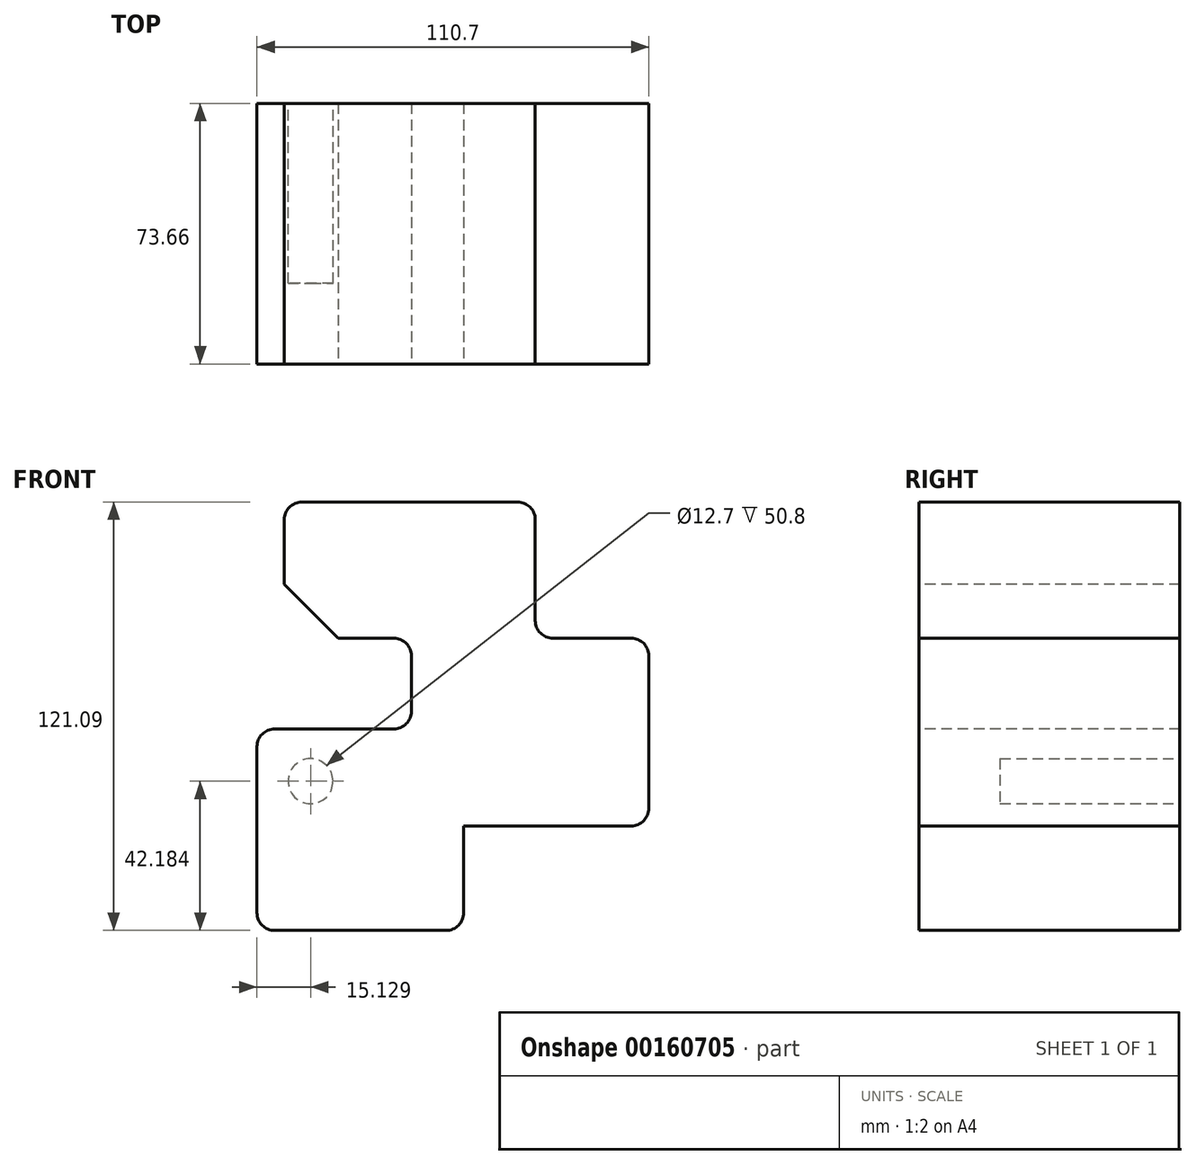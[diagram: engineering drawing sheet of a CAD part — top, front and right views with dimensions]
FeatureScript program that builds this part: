
annotation { "Feature Type Name" : "Feature", "Feature Type Description" : "" }
export const myFeature = defineFeature(function(context is Context, id is Id, definition is map)
    precondition{}
    {
        {
            var Q0;
            Q0=qCreatedBy(makeId("Front.planeOp"),FACE);
            var sketch = newSketch(context, id + "F0", { "sketchPlane" : qUnion([Q0])});
            skLineSegment(sketch, "E0", {"start": v(-32.8, 8.86) * mm, "end": v(-32.8, 47.35) * mm});
            skLineSegment(sketch, "E1", {"start": v(-32.8, 47.35) * mm, "end": v(38.1, 47.35) * mm});
            skLineSegment(sketch, "E2", {"start": v(38.1, 47.35) * mm, "end": v(38.1, 8.86) * mm});
            skLineSegment(sketch, "E3", {"start": v(38.1, 8.86) * mm, "end": v(70.2, 8.86) * mm});
            skLineSegment(sketch, "E4", {"start": v(70.2, 8.86) * mm, "end": v(70.2, -44.2) * mm});
            skLineSegment(sketch, "E5", {"start": v(70.2, -44.2) * mm, "end": v(17.9, -44.2) * mm});
            skLineSegment(sketch, "E6", {"start": v(17.9, -44.2) * mm, "end": v(17.9, -73.74) * mm});
            skLineSegment(sketch, "E7", {"start": v(17.9, -73.74) * mm, "end": v(-40.5, -73.74) * mm});
            skLineSegment(sketch, "E8", {"start": v(-40.5, -73.74) * mm, "end": v(-40.5, -16.8) * mm});
            skLineSegment(sketch, "E9", {"start": v(-40.5, -16.8) * mm, "end": v(3.13, -16.8) * mm});
            skLineSegment(sketch, "E10", {"start": v(3.13, -16.8) * mm, "end": v(3.13, 8.86) * mm});
            skLineSegment(sketch, "E11", {"start": v(3.13, 8.86) * mm, "end": v(-32.8, 8.86) * mm});
            skSolve(sketch);
        }
        {
            var Q0;
            Q0=makeQuery(id+"F0.imprint","IMPRINT",FACE,{"disambiguationData":[TD([[makeQuery(id+"F0.imprint","IMPRINT",EDGE,{"derivedFrom":sQuery(id+"F0.wireOp",EDGE,"E0")}),-1.0]])]});
            extrude(context, id + "F1", {"entities" : qUnion([Q0]), "oppositeDirection" : true, "depth" : 73.66 * mm});
        }
        {
            var Q0;
            Q0=makeQuery(id+"F1.opExtrude","SWEPT_EDGE",EDGE,{"disambiguationData":[OSD([sQuery(id+"F0.wireOp",EDGE,"E1"),sQuery(id+"F0.wireOp",EDGE,"E2")])]});
            var Q1;
            Q1=makeQuery(id+"F1.opExtrude","SWEPT_EDGE",EDGE,{"disambiguationData":[OSD([sQuery(id+"F0.wireOp",EDGE,"E0"),sQuery(id+"F0.wireOp",EDGE,"E1")])]});
            var Q2;
            Q2=makeQuery(id+"F1.opExtrude","SWEPT_EDGE",EDGE,{"disambiguationData":[OSD([sQuery(id+"F0.wireOp",EDGE,"E2"),sQuery(id+"F0.wireOp",EDGE,"E3")])]});
            var Q3;
            Q3=makeQuery(id+"F1.opExtrude","SWEPT_EDGE",EDGE,{"disambiguationData":[OSD([sQuery(id+"F0.wireOp",EDGE,"E3"),sQuery(id+"F0.wireOp",EDGE,"E4")])]});
            var Q4;
            Q4=makeQuery(id+"F1.opExtrude","SWEPT_EDGE",EDGE,{"disambiguationData":[OSD([sQuery(id+"F0.wireOp",EDGE,"E4"),sQuery(id+"F0.wireOp",EDGE,"E5")])]});
            var Q5;
            Q5=makeQuery(id+"F1.opExtrude","SWEPT_EDGE",EDGE,{"disambiguationData":[OSD([sQuery(id+"F0.wireOp",EDGE,"E6"),sQuery(id+"F0.wireOp",EDGE,"E7")])]});
            var Q6;
            Q6=makeQuery(id+"F1.opExtrude","SWEPT_EDGE",EDGE,{"disambiguationData":[OSD([sQuery(id+"F0.wireOp",EDGE,"E7"),sQuery(id+"F0.wireOp",EDGE,"E8")])]});
            var Q7;
            Q7=makeQuery(id+"F1.opExtrude","SWEPT_EDGE",EDGE,{"disambiguationData":[OSD([sQuery(id+"F0.wireOp",EDGE,"E8"),sQuery(id+"F0.wireOp",EDGE,"E9")])]});
            var Q8;
            Q8=makeQuery(id+"F1.opExtrude","SWEPT_EDGE",EDGE,{"disambiguationData":[OSD([sQuery(id+"F0.wireOp",EDGE,"E9"),sQuery(id+"F0.wireOp",EDGE,"E10")])]});
            var Q9;
            Q9=makeQuery(id+"F1.opExtrude","SWEPT_EDGE",EDGE,{"disambiguationData":[OSD([sQuery(id+"F0.wireOp",EDGE,"E10"),sQuery(id+"F0.wireOp",EDGE,"E11")])]});
            fillet(context, id + "F2", {"entities" : qUnion([Q0, Q1, Q2, Q3, Q4, Q5, Q6, Q7, Q8, Q9]), "radius" : 5 * mm, "tangentPropagation" : true, "allowEdgeOverflow" : false});
        }
        {
            var Q0;
            Q0=makeQuery(id+"F1.opExtrude","CAP_FACE",FACE,{"disambiguationData":[OSD([sQuery(id+"F0.wireOp",EDGE,"E0"),sQuery(id+"F0.wireOp",EDGE,"E1"),sQuery(id+"F0.wireOp",EDGE,"E2"),sQuery(id+"F0.wireOp",EDGE,"E3"),sQuery(id+"F0.wireOp",EDGE,"E4"),sQuery(id+"F0.wireOp",EDGE,"E5"),sQuery(id+"F0.wireOp",EDGE,"E6"),sQuery(id+"F0.wireOp",EDGE,"E7"),sQuery(id+"F0.wireOp",EDGE,"E8"),sQuery(id+"F0.wireOp",EDGE,"E9"),sQuery(id+"F0.wireOp",EDGE,"E10"),sQuery(id+"F0.wireOp",EDGE,"E11")])],"isStart":true});
            var sketch = newSketch(context, id + "F3", { "sketchPlane" : qUnion([Q0])});
            skLineSegment(sketch, "E12", {"start": v(-32.8, 8.86) * mm, "end": v(-17.57, 8.86) * mm});
            skLineSegment(sketch, "E13", {"start": v(-32.8, 8.86) * mm, "end": v(-32.8, 24.1) * mm});
            skLineSegment(sketch, "E14", {"start": v(-32.8, 24.1) * mm, "end": v(-17.57, 8.86) * mm});
            skSolve(sketch);
        }
        {
            var Q0;
            Q0=makeQuery(id+"F3.imprint","IMPRINT",FACE,{"disambiguationData":[TD([[makeQuery(id+"F3.imprint","IMPRINT",EDGE,{"derivedFrom":sQuery(id+"F3.wireOp",EDGE,"E12")}),-1.0]])]});
            extrude(context, id + "F4", {"entities" : qUnion([Q0]), "operationType" : NewBodyOperationType.REMOVE, "endBound" : BoundingType.THROUGH_ALL, "oppositeDirection" : true, "depth" : 25 * mm});
        }
        {
            var Q0;
            Q0=makeQuery(id+"F1.opExtrude","CAP_FACE",FACE,{"disambiguationData":[OSD([sQuery(id+"F0.wireOp",EDGE,"E0"),sQuery(id+"F0.wireOp",EDGE,"E1"),sQuery(id+"F0.wireOp",EDGE,"E2"),sQuery(id+"F0.wireOp",EDGE,"E3"),sQuery(id+"F0.wireOp",EDGE,"E4"),sQuery(id+"F0.wireOp",EDGE,"E5"),sQuery(id+"F0.wireOp",EDGE,"E6"),sQuery(id+"F0.wireOp",EDGE,"E7"),sQuery(id+"F0.wireOp",EDGE,"E8"),sQuery(id+"F0.wireOp",EDGE,"E9"),sQuery(id+"F0.wireOp",EDGE,"E10"),sQuery(id+"F0.wireOp",EDGE,"E11")])],"isStart":false});
            var sketch = newSketch(context, id + "F5", { "sketchPlane" : qUnion([Q0])});
            skCircle(sketch, "E15", {"center": v(25.38, -31.56) * mm, "radius": 6.35 * mm});
            skSolve(sketch);
        }
        {
            var Q0;
            Q0=makeQuery(id+"F5.imprint","IMPRINT",FACE,{"disambiguationData":[TD([[makeQuery(id+"F5.imprint","IMPRINT",EDGE,{"derivedFrom":sQuery(id+"F5.wireOp",EDGE,"E15")}),1.0]])]});
            extrude(context, id + "F6", {"entities" : qUnion([Q0]), "operationType" : NewBodyOperationType.REMOVE, "oppositeDirection" : true, "depth" : 50.8 * mm});
        }
    });
